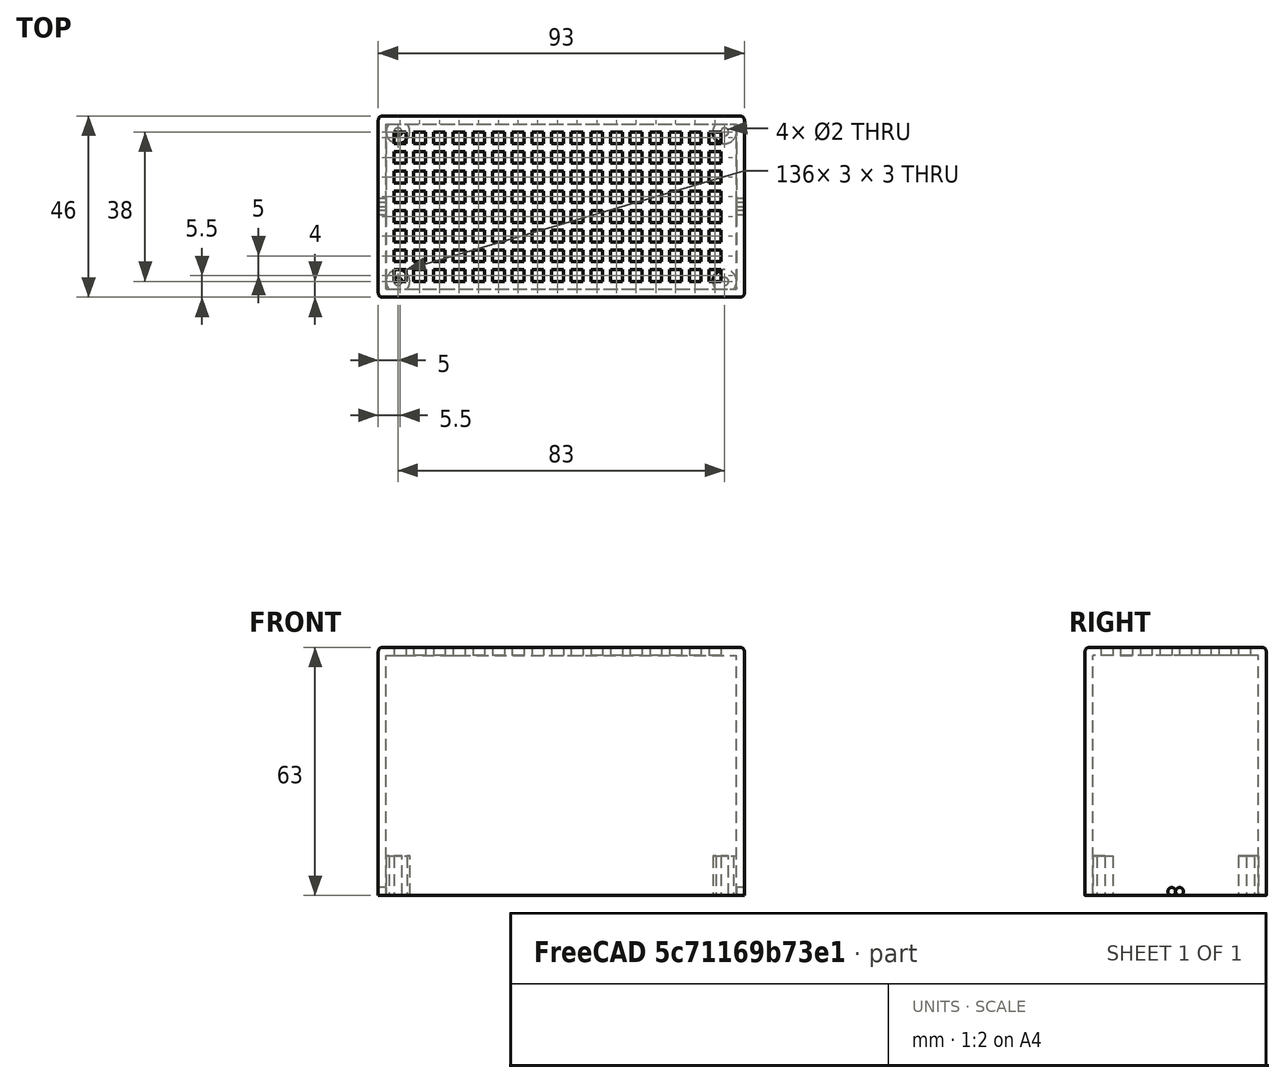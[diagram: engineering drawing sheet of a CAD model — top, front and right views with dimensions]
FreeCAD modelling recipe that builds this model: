
FCSTD DOCUMENT  (FreeCAD 0.20RUnknown)
Label: LX-2BUPS-1
License: All rights reserved
LicenseURL: https://en.wikipedia.org/wiki/All_rights_reserved
objects: Sketcher::SketchObject×3, PartDesign::Pocket×2, PartDesign::LinearPattern×2, Part::Box×1, PartDesign::FeatureBase×1, PartDesign::Thickness×1, PartDesign::Fillet×1, PartDesign::MultiTransform×1, Part::Extrusion×1, PartDesign::Body×1, Part::FeaturePython×1, Mesh::Feature×1
note: 19 computed .brp shape members not serialized (recipe doc carries the construction recipe); baked Part::Feature solids carry a one-line shape summary decoded from their .brp

FEATURE [Part::Box] Box  label="Куб"
  AttacherType = Attacher::AttachEngine3D
  Height = 60
  Length = 93
  Width = 46
FEATURE [PartDesign::FeatureBase] BaseFeature
  BaseFeature = -> Box
FEATURE [PartDesign::Thickness] Thickness
  Base = -> BaseFeature [Face5]
  BaseFeature = -> BaseFeature
  Intersection = false
  Join = 0
  Mode = 0
  Refine = true
  Reversed = true
  SupportTransform = false
  Value = 2
FEATURE [PartDesign::Fillet] Fillet
  Base = -> Thickness [Edge9,Edge8,Edge7,Edge3,Edge12,Edge2,Edge1,Edge6]
  BaseFeature = -> Thickness
  Radius = 1
  Refine = true
  SupportTransform = false
  UseAllEdges = false
FEATURE [Sketcher::SketchObject] Sketch
  FullyConstrained = true
  MapMode = 5
  Placement = pos=(0,0,63) rot=(0,0,1;0rad)
  sketch-geometry (4):
    g0: LineSegment StartX=4 StartY=7 StartZ=0 EndX=4 EndY=4 EndZ=0
    g1: LineSegment StartX=4 StartY=4 StartZ=0 EndX=7 EndY=4 EndZ=0
    g2: LineSegment StartX=7 StartY=4 StartZ=0 EndX=7 EndY=7 EndZ=0
    g3: LineSegment StartX=7 StartY=7 StartZ=0 EndX=4 EndY=7 EndZ=0
  constraints (12):
    c: Coincident(g0,g1)
    c: Coincident(g1,g2)
    c: Coincident(g2,g3)
    c: Coincident(g3,g0)
    c: Vertical(g0)
    c: Vertical(g2)
    c: Horizontal(g1)
    c: Horizontal(g3)
    c: DistanceX(g-1,g0) = 4
    c: DistanceY(g-1,g0) = 4
    c: DistanceX(g1,g1) = 3
    c: DistanceY(g0,g0) = 3
FEATURE [PartDesign::Pocket] Pocket
  BaseFeature = -> Fillet
  Direction = (0,0,-1)
  Length = 2
  Length2 = 5
  Profile = -> Sketch
  ReferenceAxis = -> Sketch [N_Axis]
  Refine = true
  Type = 0
FEATURE [PartDesign::LinearPattern] LinearPattern
  Direction = -> X_Axis
  Length = 80
  Occurrences = 17
  Refine = true
FEATURE [PartDesign::LinearPattern] LinearPattern001
  Direction = -> Y_Axis
  Length = 35
  Occurrences = 8
  Refine = true
FEATURE [PartDesign::MultiTransform] MultiTransform
  BaseFeature = -> Pocket
  Originals = -> [Pocket]
  Refine = true
  Transformations = -> [LinearPattern,LinearPattern001]
FEATURE [Sketcher::SketchObject] Sketch001
  FullyConstrained = true
  MapMode = 5
  Placement = pos=(0,0,0) rot=(1,0,0;3.14159rad)
  Support = -> [MultiTransform]
  sketch-geometry (8):
    g0: Circle CenterX=5 CenterY=-42 CenterZ=0 NormalX=0 NormalY=0 NormalZ=1 AngleXU=0 Radius=1
    g1: Circle CenterX=5 CenterY=-42 CenterZ=0 NormalX=0 NormalY=0 NormalZ=1 AngleXU=0 Radius=3
    g2: Circle CenterX=5 CenterY=-4 CenterZ=0 NormalX=0 NormalY=0 NormalZ=1 AngleXU=0 Radius=1
    g3: Circle CenterX=5 CenterY=-4 CenterZ=0 NormalX=0 NormalY=0 NormalZ=1 AngleXU=0 Radius=3
    g4: Circle CenterX=88 CenterY=-4 CenterZ=0 NormalX=0 NormalY=0 NormalZ=1 AngleXU=0 Radius=1
    g5: Circle CenterX=88 CenterY=-4 CenterZ=0 NormalX=0 NormalY=0 NormalZ=1 AngleXU=0 Radius=3
    g6: Circle CenterX=88 CenterY=-42 CenterZ=0 NormalX=0 NormalY=0 NormalZ=1 AngleXU=0 Radius=1
    g7: Circle CenterX=88 CenterY=-42 CenterZ=0 NormalX=0 NormalY=0 NormalZ=1 AngleXU=0 Radius=3
  constraints (20):
    c: Radius(g0) = 1
    c: Radius(g1) = 3
    c: DistanceX(g0) = 5
    c: DistanceY(g0) = -42
    c: Coincident(g1,g0)
    c: Coincident(g3,g2)
    c: Radius(g2) = 1
    c: Radius(g3) = 3
    c: DistanceY(g2) = -4
    c: Vertical(g2,g0)
    c: Coincident(g5,g4)
    c: Radius(g4) = 1
    c: Radius(g5) = 3
    c: DistanceX(g4) = 88
    c: Coincident(g7,g6)
    c: Radius(g6) = 1
    c: Radius(g7) = 3
    c: Horizontal(g6,g0)
    c: Vertical(g6,g4)
    c: Horizontal(g4,g2)
FEATURE [Part::Extrusion] Extrude002
  Base = -> Sketch001
  Dir = (0,0,1)
  DirMode = 0
  FaceMakerClass = Part::FaceMakerBullseye
  LengthFwd = 10
  LengthRev = 0
  Solid = true
  Symmetric = false
FEATURE [Sketcher::SketchObject] Sketch002
  FullyConstrained = true
  MapMode = 5
  Placement = pos=(0,0,0) rot=(0.57735,-0.57735,-0.57735;2.0944rad)
  Support = -> [MultiTransform]
  sketch-geometry (2):
    g0: Circle CenterX=-22 CenterY=1 CenterZ=0 NormalX=0 NormalY=0 NormalZ=1 AngleXU=0 Radius=1
    g1: Circle CenterX=-24 CenterY=1 CenterZ=0 NormalX=0 NormalY=0 NormalZ=1 AngleXU=0 Radius=1
  constraints (6):
    c: Radius(g0) = 1
    c: Radius(g1) = 1
    c: Horizontal(g0,g1)
    c: DistanceX(g0) = -22
    c: DistanceX(g1) = -24
    c: DistanceY(g1) = 1
FEATURE [PartDesign::Pocket] Pocket001
  BaseFeature = -> MultiTransform
  Direction = (1,0,0)
  Length = 100
  Length2 = 5
  Profile = -> Sketch002
  ReferenceAxis = -> Sketch002 [N_Axis]
  Type = 0
FEATURE [PartDesign::Body] Body
  BaseFeature = -> Box
  Group = -> [BaseFeature,Thickness,Fillet,Sketch,Pocket,MultiTransform,LinearPattern,LinearPattern001,Sketch001,Sketch002,Pocket001]
  Origin = -> Origin
  Tip = -> Pocket001
FEATURE [Part::FeaturePython] Connect  # WARN: FeaturePython — macro-defined, semantics opaque (R4)
  Objects = -> [Body,Extrude002]
  Tolerance = 0
FEATURE [Mesh::Feature] Mesh  label="Connect (Meshed)"
